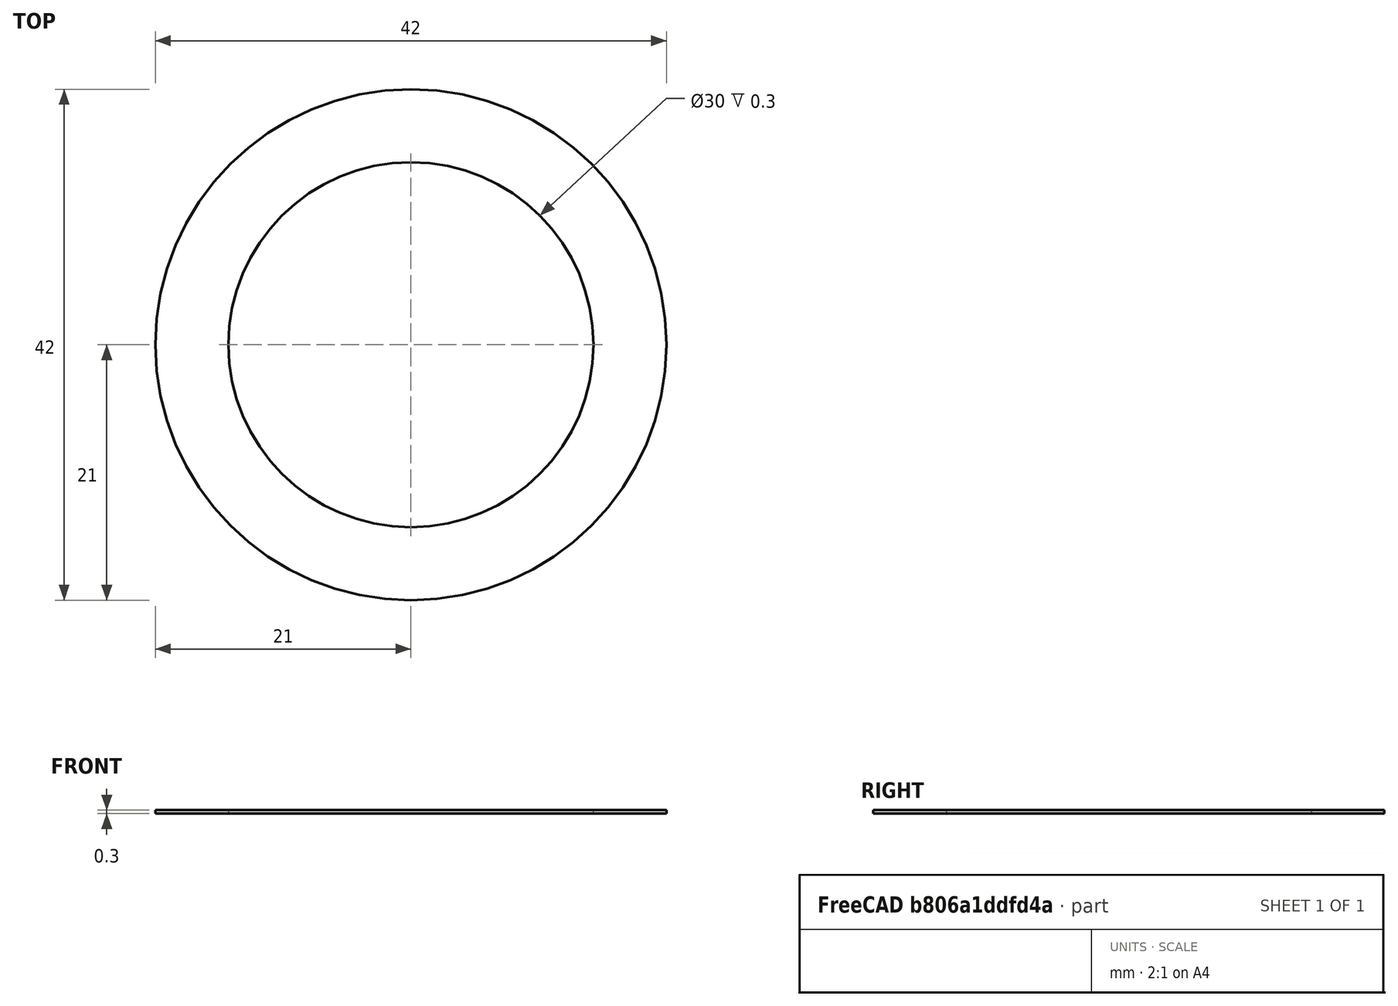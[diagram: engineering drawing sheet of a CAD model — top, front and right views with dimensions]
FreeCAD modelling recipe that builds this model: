
FCSTD DOCUMENT  (FreeCAD 0.19R24366 (Git))
Label: 30 x 42 x 0_3mm shim washer
License: All rights reserved
LicenseURL: http://en.wikipedia.org/wiki/All_rights_reserved
objects: Sketcher::SketchObject×1, PartDesign::Pad×1, PartDesign::Body×1
note: 4 computed .brp shape members not serialized (recipe doc carries the construction recipe); baked Part::Feature solids carry a one-line shape summary decoded from their .brp

FEATURE [Sketcher::SketchObject] Sketch
  FullyConstrained = true
  MapMode = 5
  Support = -> [XY_Plane]
  sketch-geometry (2):
    g0: Circle CenterX=0 CenterY=0 CenterZ=0 NormalX=0 NormalY=0 NormalZ=1 AngleXU=0 Radius=15
    g1: Circle CenterX=0 CenterY=0 CenterZ=0 NormalX=0 NormalY=0 NormalZ=1 AngleXU=0 Radius=21
  constraints (4):
    c: Coincident(g0,g-1)
    c: Coincident(g1,g0)
    c: Diameter(g0) = 30
    c: Diameter(g1) = 42
FEATURE [PartDesign::Pad] Pad
  Direction = (1,1,1)
  Length = 0.3
  Length2 = 100
  Profile = -> Sketch
  Type = 0
FEATURE [PartDesign::Body] Body
  Group = -> [Sketch,Pad]
  Origin = -> Origin
  Tip = -> Pad
